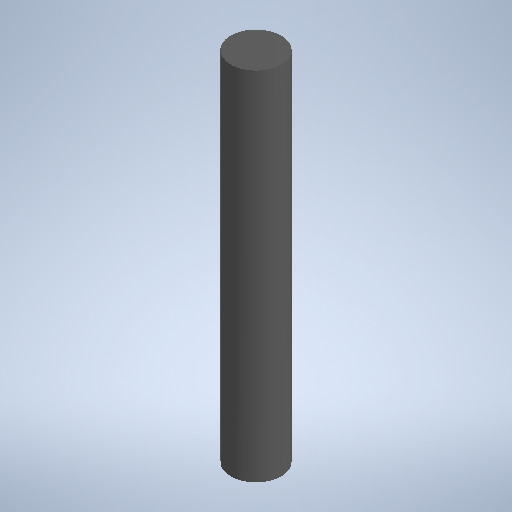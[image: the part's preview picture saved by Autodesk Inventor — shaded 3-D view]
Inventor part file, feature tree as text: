
AUTODESK INVENTOR PART (.ipt)
format: ipt  version: 2025.1 (Build 291241020, 241B)  size: 215,552 bytes
history: native  units: mm (DEFAULTED — no unit token found)
features: extrude x1, sketch x1
ambient origin geometry x8: Origin, YZ Plane, XZ Plane, XY Plane, X Axis, Y Axis, Z Axis, Center Point
bodies: Solid1 (feature_tree)
feature tree (2):
  extrude  "Extrusion1"  Depth=17.5mm TaperAngle=0.0deg
  sketch  "Sketch1"  dims[d0=2.475mm d1=17.5mm d2=0.0mm]
